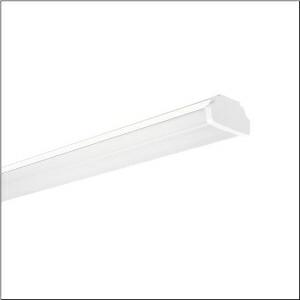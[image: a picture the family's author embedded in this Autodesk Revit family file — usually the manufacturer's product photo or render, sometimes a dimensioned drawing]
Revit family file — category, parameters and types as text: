
# Revit family: modario_r__31_ho_53bm811m1v4120_5d14
name_source: partatom
category: Lighting Fixtures
units: mm (PartAtom-declared; Revit-internal decimal feet)

## family parameters
Cut with Voids When Loaded = No
Host = Face
Light Source = No
Part Type = Normal
Room Calculation Point = No
Round Connector Dimension = Use Diameter
Shared = No

## types (1)
- --- (1 x LED, 12380 lm, 77.3 W, 4000K)
    Apparent Load = 77 VA
    CIE Flux Codes = 52 78 94 90 100
    Color Rendering = 80
    Color Temperature = 4000K
    Default Elevation = 1800 mm
    Description = Modario® 31 HO, luminaire insert, of sheet steel, coil coated, white, length: 1.495mm, width: 81mm, height: 82mm, 5x system unit, system units: 299mm, LED rated luminous flux: 12.380lm, light colour: 840, control gear: ON/OFF Multilumen, control gear: ECG Multilumen, with plug, 3-pole, with phase selection, mains connection: 220..240V, AC, 50/60Hz, rated input power: 77W, through-wiring accessed according to module size, primary optical cover: cover, of PMMA, light emission: direct distribution, primary light characteristic: symmetric, protection rating (complete): IP20, protection rating (LED compartment): IP50, insulation class (complete): insulation class I (protective earthing), certification: CE, ENEC, VDE, UKCA, impact resistance: IK03, permissible ambient temperature for indoor applications: -35..+35°C, corresponds to IFS (International Featured Standards) requirements for safety and quality in the food industry, reducing of maximum allowable ambient temperature of 5°C with ceiling mounting, packaging unit: 1 piece
    Height = 92 mm
    Lamp = 1 x LED
    Lamp Light Flux = 12380 lm
    Lamp Power = 77.3 W
    Lamp count = 1
    Length = 1495 mm
    Luminous efficacy = 160 lm/W
    Manufacturer = Siteco
    ModVariant = No
    Model = 53BM811M1V4120
    Mounting Place = Ceiling
    Mounting Type = Pendant
    Number of Poles = 1
    OnlyDefault = Yes
    Power Factor = 1
    Product Name = Modario® 31 HO
    Product group = luminaire insert | ceiling pendant
    ProductGroupID = 902
    Protection Class = Protection class I
    Protection Degree = IP 20
    RLX_Detail_Level = 1
    RLX_Emergency_Light_Flux = 0 lm
    RLX_Emergency_Type = 0
    RLX_Emergency_Type_DB = No
    RlxData = <blob elided: 40101 chars, md5=8d991db6>
    Socket = socket
    Standby Power = 0 W
    System Light Flux = 12380 lm
    System Power = 77 W
    Type Comments = factory setting: luminous flux: 100 % | (A | C | E) | 173 mA
    Type Image = l_1341886.jpg
    URL = http://relux.com
    VarID = @adj_218685
    Voltage = 0 V
    Weight = 0.00 kg
    Width = 81 mm

## geometry (parser evidence)
native form markers: Blend x4, Sweep x11
no freeform markers — native parametric forms only
